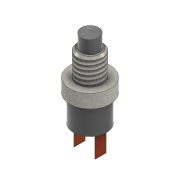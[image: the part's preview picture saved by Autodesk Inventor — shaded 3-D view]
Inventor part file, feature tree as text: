
AUTODESK INVENTOR PART (.ipt)
format: ipt  version: 2022.3 (Build 263350000, 350)  size: 147,968 bytes
history: native  units: mm
features: extrude x5, sketch x5, chamfer x2, other x1, thread x1
ambient origin geometry x8: Origin, YZ Plane, XZ Plane, XY Plane, X Axis, Y Axis, Z Axis, Center Point
bodies: Body1 (feature_tree)
feature tree (14):
  other  "Sólido1"
  extrude  "Extrusión1"  Depth=6.0mm TaperAngle=0.0deg
  extrude  "Extrusión2"  Depth=3.6mm TaperAngle=0.0deg
  chamfer  "Chaflán1"  Distance=2.0mm Angle=45.0deg
  extrude  "Extrusión3"  Depth=3.2mm TaperAngle=0.0deg
  extrude  "Extrusión4"  Depth=6.25mm TaperAngle=0.0deg
  thread  "Rosca1"  [1 undecoded]
  chamfer  "Chaflán2"  Distance=0.5mm Angle=45.0deg
  extrude  "Extrusión5"  Depth=5.5mm
  sketch  "Boceto1"  dims[d0=6.0mm d1=6.0mm d2=0.0mm]
  sketch  "Boceto2"  dims[d3=4.15mm d4=3.6mm d5=0.0mm d6=2.0mm d7=0.5mm d8=45.0deg]
  sketch  "Boceto3"  dims[d9=9.55mm d10=3.2mm d11=0.0mm]
  sketch  "Boceto4"  dims[d12=7.85mm d13=6.25mm d14=0.0mm d15=6.2mm d16=0.0mm d17=0.5mm d18=0.5mm d19=45.0deg]
  sketch  "Boceto5"  dims[d20=2.5mm d21=2.5mm d22=0.1mm d23=2.55mm d24=0.1mm d25=5.5mm d26=0.0mm]
note: 1 required parameter value undecoded (feature->parameter linkage not recoverable at this tier; creation-order binding heuristic only, values carry confidence <= 0.55)
